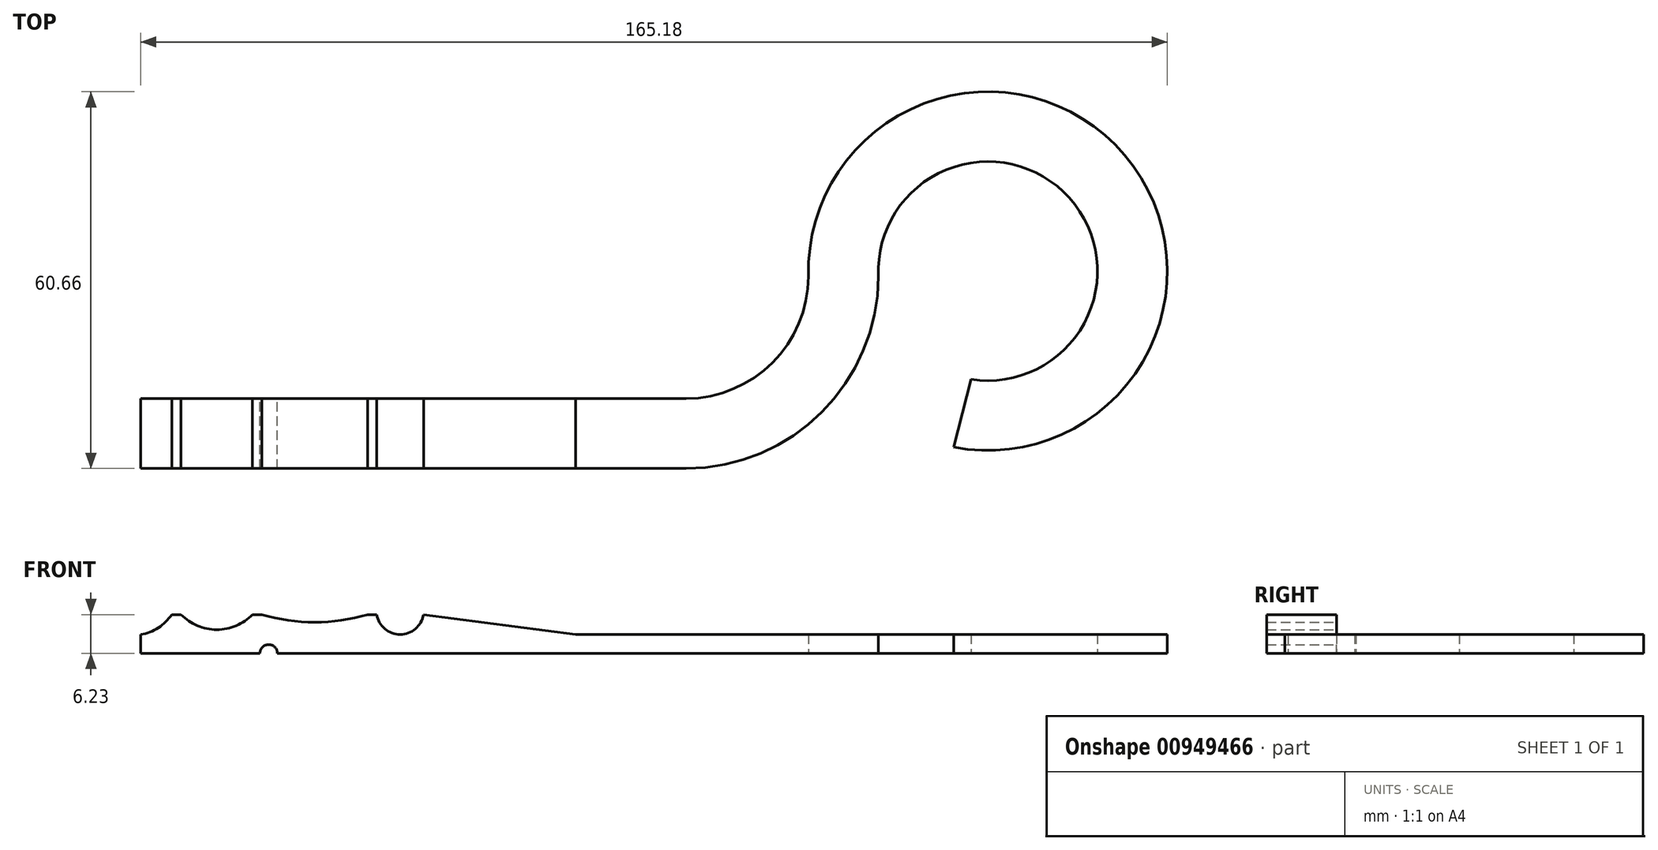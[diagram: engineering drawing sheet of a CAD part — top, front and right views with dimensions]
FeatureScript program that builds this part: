
annotation { "Feature Type Name" : "Feature", "Feature Type Description" : "" }
export const myFeature = defineFeature(function(context is Context, id is Id, definition is map)
    precondition{}
    {
        {
            var Q0;
            Q0=qCreatedBy(makeId("Front.planeOp"),FACE);
            var sketch = newSketch(context, id + "F0", { "sketchPlane" : qUnion([Q0])});
            skLineSegment(sketch, "E0.top", {"start": v(-84.17, 7.43) * mm, "end": v(-14.17, 7.43) * mm, "construction": true});
            skLineSegment(sketch, "E0.left", {"start": v(-84.17, 10.43) * mm, "end": v(-84.17, 7.43) * mm});
            skLineSegment(sketch, "E0.right", {"start": v(-14.17, 10.43) * mm, "end": v(-14.17, 7.43) * mm});
            skLineSegment(sketch, "E1", {"start": v(-91.89, 13.66) * mm, "end": v(-12.1, 13.66) * mm, "construction": true});
            skArc(sketch, "E2", {"start": v(-84.17, 10.43) * mm, "mid": v(-81.33, 11.52) * mm, "end": v(-79.17, 13.66) * mm});
            skArc(sketch, "E3", {"start": v(-64.67, 13.66) * mm, "mid": v(-56.17, 12.43) * mm, "end": v(-47.67, 13.66) * mm});
            skLineSegment(sketch, "E4", {"start": v(-38.67, 13.66) * mm, "end": v(-14.17, 10.43) * mm});
            skLineSegment(sketch, "E5", {"start": v(-79.17, 13.66) * mm, "end": v(-77.67, 13.66) * mm});
            skLineSegment(sketch, "E6", {"start": v(-64.67, 13.66) * mm, "end": v(-66.17, 13.66) * mm});
            skLineSegment(sketch, "E7", {"start": v(-47.67, 13.66) * mm, "end": v(-46.17, 13.66) * mm});
            skArc(sketch, "E8", {"start": v(-77.67, 13.66) * mm, "mid": v(-71.92, 11.23) * mm, "end": v(-66.17, 13.66) * mm});
            skArc(sketch, "E9", {"start": v(-46.17, 13.66) * mm, "mid": v(-42.42, 10.47) * mm, "end": v(-38.67, 13.66) * mm});
            skLineSegment(sketch, "E10", {"start": v(-84.17, 7.43) * mm, "end": v(-64.97, 7.43) * mm});
            skLineSegment(sketch, "E11", {"start": v(-14.17, 7.43) * mm, "end": v(-62.17, 7.43) * mm});
            skArc(sketch, "E12", {"start": v(-62.17, 7.43) * mm, "mid": v(-63.57, 8.83) * mm, "end": v(-64.97, 7.43) * mm});
            skSolve(sketch);
        }
        {
            var Q0;
            Q0=qSketchRegion(id+"F0",true);
            extrude(context, id + "F1", {"entities" : qUnion([Q0]), "depth" : 11.25 * mm, "offsetDistance" : 25 * mm});
        }
        {
            var Q0;
            Q0=makeQuery(id+"F1.opExtrude","SWEPT_FACE",FACE,{"disambiguationData":[OSD([sQuery(id+"F0.wireOp",EDGE,"E11")])]});
            var sketch = newSketch(context, id + "F2", { "sketchPlane" : qUnion([Q0])});
            skLineSegment(sketch, "E13", {"start": v(-25.6, 0) * mm, "end": v(-25.6, 11.25) * mm});
            skLineSegment(sketch, "E14", {"start": v(-25.6, 11.25) * mm, "end": v(3.57, 11.25) * mm});
            skLineSegment(sketch, "E15", {"start": v(-25.6, 0) * mm, "end": v(3.57, 0) * mm});
            skArc(sketch, "E16", {"start": v(23.28, -19.7) * mm, "mid": v(17.47, -5.8) * mm, "end": v(3.57, 0) * mm});
            skArc(sketch, "E17", {"start": v(23.28, -19.7) * mm, "mid": v(74.15, -39.2) * mm, "end": v(46.61, 7.8) * mm});
            skArc(sketch, "E18", {"start": v(34.53, -19.7) * mm, "mid": v(25.43, 2.15) * mm, "end": v(3.57, 11.25) * mm});
            skArc(sketch, "E19", {"start": v(34.53, -19.7) * mm, "mid": v(65.25, -32.32) * mm, "end": v(49.44, -3.1) * mm});
            skLineSegment(sketch, "E20", {"start": v(49.44, -3.1) * mm, "end": v(46.61, 7.8) * mm});
            skLineSegment(sketch, "E21", {"start": v(13.33, -19.7) * mm, "end": v(43.23, -19.7) * mm, "construction": true});
            skSolve(sketch);
        }
        {
            var Q0;
            Q0 = qSketchRegion(id + "F2", true);
            extrude(context, id + "F3", {"entities" : qUnion([Q0]), "operationType" : NewBodyOperationType.ADD, "oppositeDirection" : true, "depth" : 3 * mm, "offsetDistance" : 25 * mm});
        }
    });
